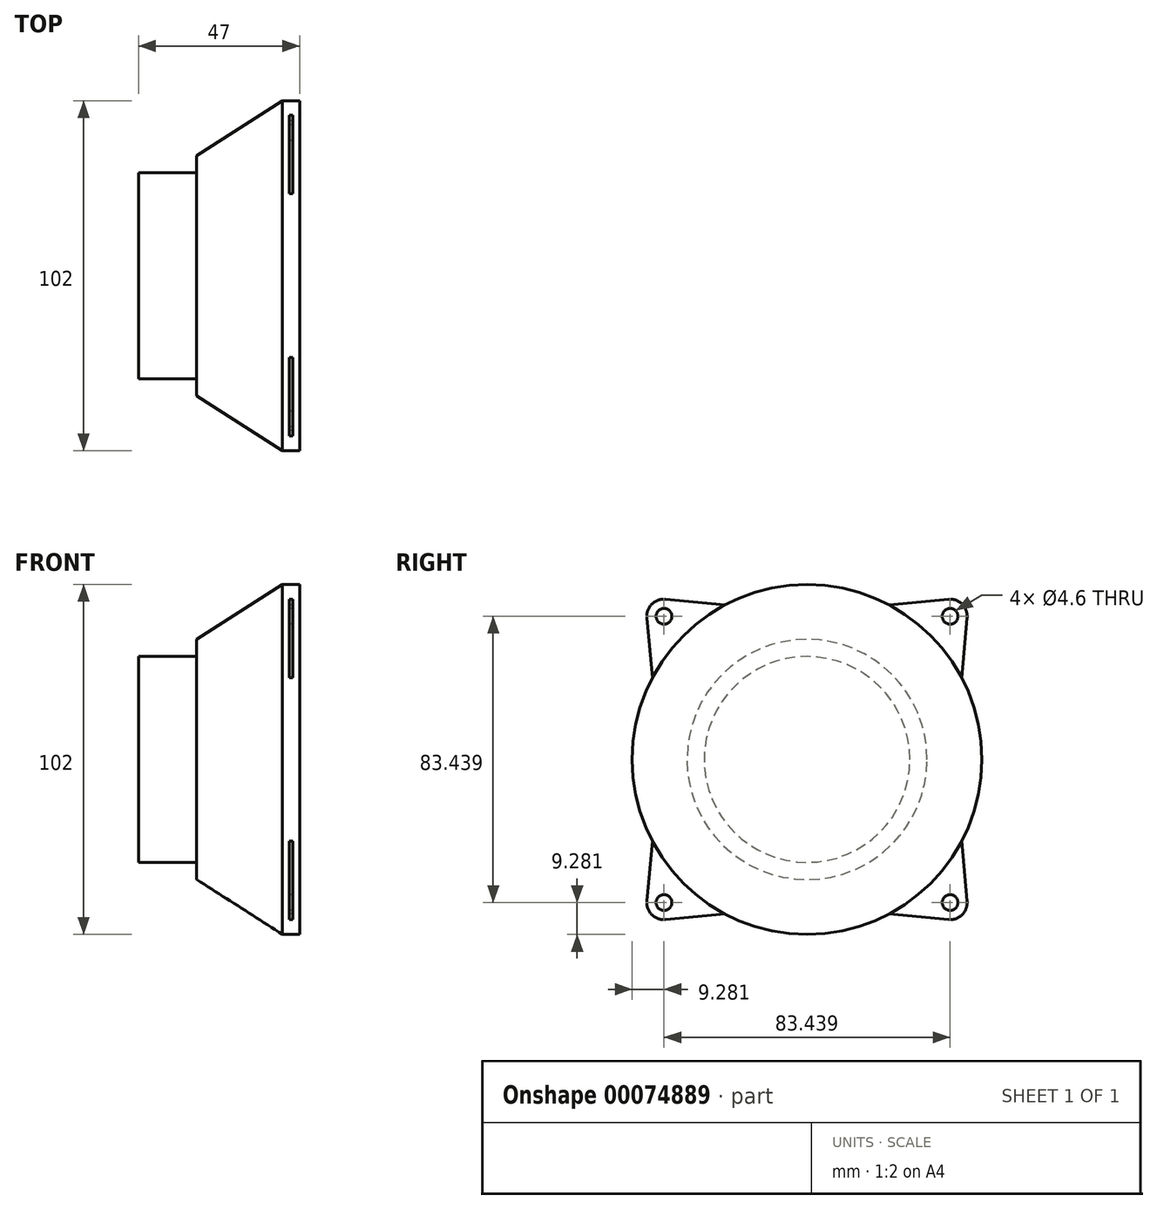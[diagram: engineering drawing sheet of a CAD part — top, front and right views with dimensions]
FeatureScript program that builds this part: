
annotation { "Feature Type Name" : "Feature", "Feature Type Description" : "" }
export const myFeature = defineFeature(function(context is Context, id is Id, definition is map)
    precondition{}
    {
        {
            var Q0;
            Q0=qCreatedBy(makeId("Right.planeOp"),FACE);
            var sketch = newSketch(context, id + "F0", { "sketchPlane" : qUnion([Q0])});
            skCircle(sketch, "E0", {"center": v(0, 0) * mm, "radius": 30 * mm});
            skCircle(sketch, "E1", {"center": v(0, 0) * mm, "radius": 51 * mm});
            skLineSegment(sketch, "E2", {"start": v(0, 0) * mm, "end": v(45.25, 45.25) * mm, "construction": true});
            skCircle(sketch, "E3", {"center": v(41.72, 41.72) * mm, "radius": 2.3 * mm});
            skArc(sketch, "E4", {"start": v(46.7, 41.25) * mm, "mid": v(45.25, 45.25) * mm, "end": v(41.25, 46.7) * mm});
            skLineSegment(sketch, "E5", {"start": v(46.7, 41.25) * mm, "end": v(45.07, 23.86) * mm});
            skLineSegment(sketch, "E6", {"start": v(41.25, 46.7) * mm, "end": v(23.86, 45.07) * mm});
            skLineSegment(sketch, "E7", {"start": v(23.86, 45.07) * mm, "end": v(45.07, 23.86) * mm, "construction": true});
            skPoint(sketch, "E8", {"position": v(34.47, 34.47) * mm});
            skLineSegment(sketch, "E9.1.0", {"start": v(-46.7, 41.25) * mm, "end": v(-45.07, 23.86) * mm});
            skArc(sketch, "E9.1.1", {"start": v(-41.25, 46.7) * mm, "mid": v(-45.25, 45.25) * mm, "end": v(-46.7, 41.25) * mm});
            skLineSegment(sketch, "E9.1.2", {"start": v(-41.25, 46.7) * mm, "end": v(-23.86, 45.07) * mm});
            skCircle(sketch, "E9.1.3", {"center": v(-41.72, 41.72) * mm, "radius": 2.3 * mm});
            skLineSegment(sketch, "E9.1.4", {"start": v(0, 0) * mm, "end": v(-45.25, 45.25) * mm, "construction": true});
            skLineSegment(sketch, "E9.2.0", {"start": v(-41.25, -46.7) * mm, "end": v(-23.86, -45.07) * mm});
            skArc(sketch, "E9.2.1", {"start": v(-46.7, -41.25) * mm, "mid": v(-45.25, -45.25) * mm, "end": v(-41.25, -46.7) * mm});
            skLineSegment(sketch, "E9.2.2", {"start": v(-46.7, -41.25) * mm, "end": v(-45.07, -23.86) * mm});
            skCircle(sketch, "E9.2.3", {"center": v(-41.72, -41.72) * mm, "radius": 2.3 * mm});
            skLineSegment(sketch, "E9.2.4", {"start": v(0, 0) * mm, "end": v(-45.25, -45.25) * mm, "construction": true});
            skLineSegment(sketch, "E9.3.0", {"start": v(46.7, -41.25) * mm, "end": v(45.07, -23.86) * mm});
            skArc(sketch, "E9.3.1", {"start": v(41.25, -46.7) * mm, "mid": v(45.25, -45.25) * mm, "end": v(46.7, -41.25) * mm});
            skLineSegment(sketch, "E9.3.2", {"start": v(41.25, -46.7) * mm, "end": v(23.86, -45.07) * mm});
            skCircle(sketch, "E9.3.3", {"center": v(41.72, -41.72) * mm, "radius": 2.3 * mm});
            skLineSegment(sketch, "E9.3.4", {"start": v(0, 0) * mm, "end": v(45.25, -45.25) * mm, "construction": true});
            skSolve(sketch);
        }
        {
            var Q0;
            Q0=makeQuery(id+"F0.imprint","IMPRINT",FACE,{"disambiguationData":[TD([[makeQuery(id+"F0.imprint","IMPRINT",EDGE,{"derivedFrom":sQuery(id+"F0.wireOp",EDGE,"E0")}),-1.0]])]});
            var Q1;
            Q1=makeQuery(id+"F0.imprint","IMPRINT",FACE,{"disambiguationData":[TD([[makeQuery(id+"F0.imprint","IMPRINT",EDGE,{"derivedFrom":sQuery(id+"F0.wireOp",EDGE,"E0")}),1.0]])]});
            extrude(context, id + "F1", {"entities" : qUnion([Q0, Q1]), "depth" : 30 * mm});
        }
        {
            var Q0;
            Q0=makeQuery(id+"F0.imprint","IMPRINT",FACE,{"disambiguationData":[TD([[makeQuery(id+"F0.imprint","IMPRINT",EDGE,{"derivedFrom":sQuery(id+"F0.wireOp",EDGE,"E3")}),-1.0]])]});
            var Q1;
            {var subQ1=sQuery(id+"F0.wireOp",EDGE,"E9.1.0");Q1=makeQuery(id+"F0.imprint","IMPRINT",FACE,{"disambiguationData":[TD([[makeQuery(id+"F0.imprint","IMPRINT",EDGE,{"derivedFrom":subQ1}),1.0]])]});}
            var Q2;
            {var subQ0=sQuery(id+"F0.wireOp",EDGE,"E9.2.0");Q2=makeQuery(id+"F0.imprint","IMPRINT",FACE,{"disambiguationData":[TD([[makeQuery(id+"F0.imprint","IMPRINT",EDGE,{"derivedFrom":subQ0}),1.0]])]});}
            var Q3;
            {var subQ1=sQuery(id+"F0.wireOp",EDGE,"E9.3.0");Q3=makeQuery(id+"F0.imprint","IMPRINT",FACE,{"disambiguationData":[TD([[makeQuery(id+"F0.imprint","IMPRINT",EDGE,{"derivedFrom":subQ1}),1.0]])]});}
            extrude(context, id + "F2", {"entities" : qUnion([Q0, Q1, Q2, Q3]), "operationType" : NewBodyOperationType.ADD, "depth" : 28 * mm, "hasSecondDirection" : true, "secondDirectionOppositeDirection" : false, "secondDirectionDepth" : 27 * mm});
        }
        {
            var Q0;
            Q0=makeQuery(id+"F0.imprint","IMPRINT",FACE,{"disambiguationData":[TD([[makeQuery(id+"F0.imprint","IMPRINT",EDGE,{"derivedFrom":sQuery(id+"F0.wireOp",EDGE,"E0")}),1.0]])]});
            extrude(context, id + "F3", {"entities" : qUnion([Q0]), "operationType" : NewBodyOperationType.ADD, "oppositeDirection" : true, "depth" : 17 * mm});
        }
        {
            var Q0;
            Q0=makeQuery(id+"F1.opExtrude","CAP_EDGE",EDGE,{"disambiguationData":[OSD([sQuery(id+"F0.wireOp",EDGE,"E1")])],"isStart":true});
            chamfer(context, id + "F4", {"entities" : qUnion([Q0]), "chamferType" : ChamferType.TWO_OFFSETS, "width1" : 25 * mm, "oppositeDirection" : false, "width2" : 16 * mm, "tangentPropagation" : true});
        }
    });
